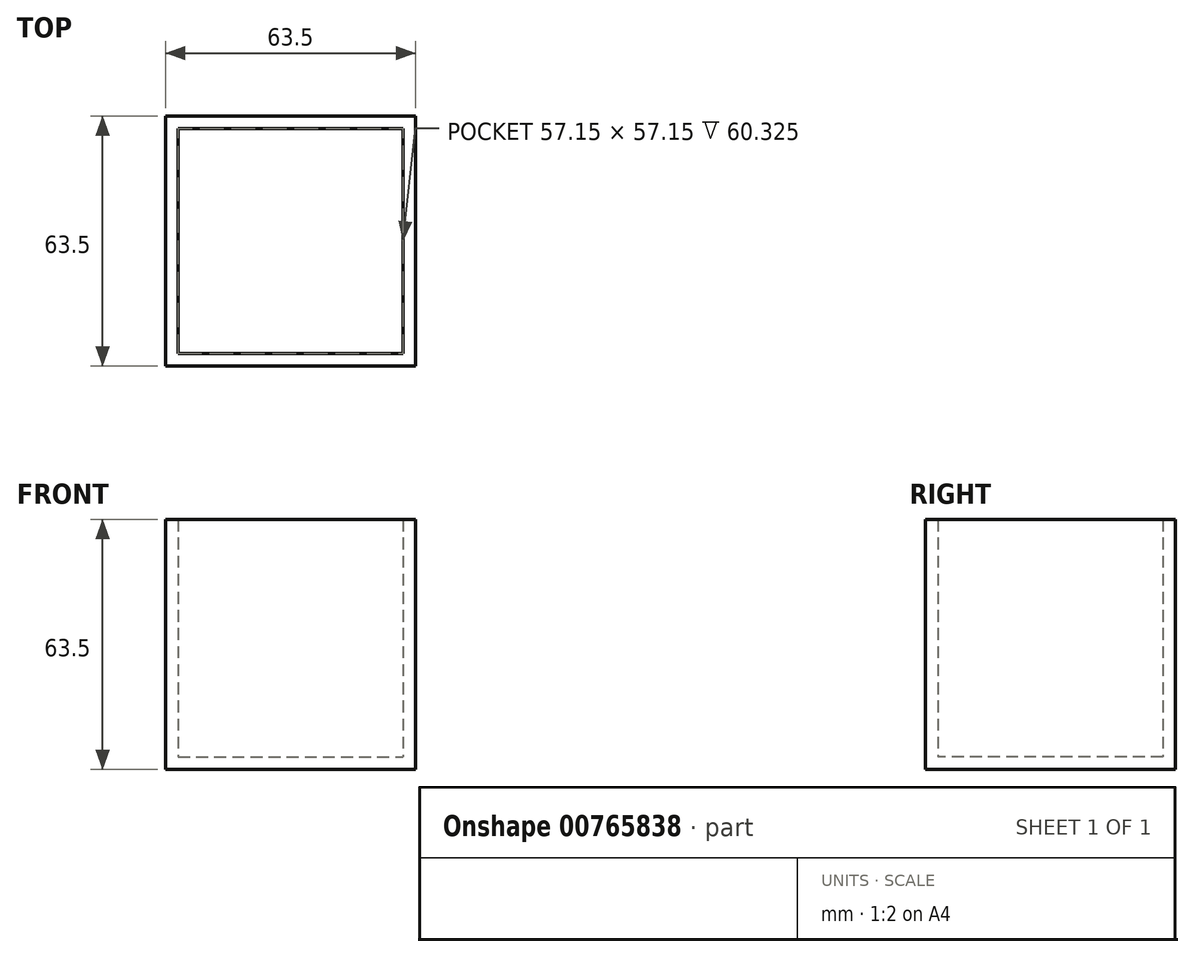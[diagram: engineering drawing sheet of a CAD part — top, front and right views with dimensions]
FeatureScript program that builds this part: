
annotation { "Feature Type Name" : "Feature", "Feature Type Description" : "" }
export const myFeature = defineFeature(function(context is Context, id is Id, definition is map)
    precondition{}
    {
        {
            var Q0;
            Q0=qCreatedBy(makeId("Top.planeOp"),FACE);
            var sketch = newSketch(context, id + "F0", { "sketchPlane" : qUnion([Q0])});
            skLineSegment(sketch, "E0.bottom", {"start": v(-31.75, 0) * mm, "end": v(31.75, 0) * mm});
            skLineSegment(sketch, "E0.top", {"start": v(-31.75, -63.5) * mm, "end": v(31.75, -63.5) * mm});
            skLineSegment(sketch, "E0.left", {"start": v(-31.75, 0) * mm, "end": v(-31.75, -63.5) * mm});
            skLineSegment(sketch, "E0.right", {"start": v(31.75, 0) * mm, "end": v(31.75, -63.5) * mm});
            skLineSegment(sketch, "E1", {"start": v(-31.75, -3.18) * mm, "end": v(31.75, -3.18) * mm});
            skLineSegment(sketch, "E2", {"start": v(-28.58, -3.18) * mm, "end": v(-28.57, -63.5) * mm});
            skLineSegment(sketch, "E3", {"start": v(28.58, -3.18) * mm, "end": v(28.58, -61.6) * mm});
            skLineSegment(sketch, "E4", {"start": v(-31.75, -60.33) * mm, "end": v(31.75, -60.33) * mm});
            skSolve(sketch);
        }
        {
            var Q0;
            {var subQ0=sQuery(id+"F0.wireOp",EDGE,"E2");var subQ1=sQuery(id+"F0.wireOp",EDGE,"E1");var subQ2=makeQuery(id+"F0.imprint","INTERSECT",VERTEX,{"derivedFrom":[subQ1,subQ0]});Q0=makeQuery(id+"F0.imprint","IMPRINT",FACE,{"disambiguationData":[TD([[makeQuery(id+"F0.imprint","IMPRINT",EDGE,{"disambiguationData":[TD([[subQ2,-1.0]])],"derivedFrom":subQ1}),-1.0]])]});}
            extrude(context, id + "F1", {"entities" : qUnion([Q0]), "depth" : 3.17 * mm, "offsetDistance" : 25.4 * mm});
        }
        {
            var Q0;
            {var subQ5=sQuery(id+"F0.wireOp",EDGE,"E0.bottom");Q0=makeQuery(id+"F0.imprint","IMPRINT",FACE,{"disambiguationData":[TD([[makeQuery(id+"F0.imprint","IMPRINT",EDGE,{"derivedFrom":subQ5}),-1.0]])]});}
            extrude(context, id + "F2", {"entities" : qUnion([Q0]), "operationType" : NewBodyOperationType.ADD, "depth" : 63.5 * mm, "offsetDistance" : 25.4 * mm});
        }
        {
            var Q0;
            {var subQ0=sQuery(id+"F0.wireOp",EDGE,"E1");var subQ1=sQuery(id+"F0.wireOp",EDGE,"E0.left");var subQ2=makeQuery(id+"F0.imprint","INTERSECT",VERTEX,{"derivedFrom":[subQ1,subQ0]});Q0=makeQuery(id+"F0.imprint","IMPRINT",FACE,{"disambiguationData":[TD([[makeQuery(id+"F0.imprint","IMPRINT",EDGE,{"disambiguationData":[TD([[subQ2,-1.0]])],"derivedFrom":subQ1}),1.0]])]});}
            var Q1;
            {var subQ0=sQuery(id+"F0.wireOp",EDGE,"E0.left");var subQ1=sQuery(id+"F0.wireOp",EDGE,"E0.top");var subQ2=makeQuery(id+"F0.imprint","INTERSECT",VERTEX,{"derivedFrom":[subQ1,subQ0]});Q1=makeQuery(id+"F0.imprint","IMPRINT",FACE,{"disambiguationData":[TD([[makeQuery(id+"F0.imprint","IMPRINT",EDGE,{"disambiguationData":[TD([[subQ2,-1.0]])],"derivedFrom":subQ1}),1.0]])]});}
            extrude(context, id + "F3", {"entities" : qUnion([Q0, Q1]), "operationType" : NewBodyOperationType.ADD, "depth" : 63.5 * mm, "offsetDistance" : 25.4 * mm});
        }
        {
            var Q0;
            {var subQ4=sQuery(id+"F0.wireOp",EDGE,"E0.top");var subQ6=sQuery(id+"F0.wireOp",EDGE,"E0.right");var subQ7=makeQuery(id+"F0.imprint","INTERSECT",VERTEX,{"derivedFrom":[subQ4,subQ6]});Q0=makeQuery(id+"F0.imprint","IMPRINT",FACE,{"disambiguationData":[TD([[makeQuery(id+"F0.imprint","IMPRINT",EDGE,{"disambiguationData":[TD([[subQ7,1.0]])],"derivedFrom":subQ4}),1.0]])]});}
            extrude(context, id + "F4", {"entities" : qUnion([Q0]), "operationType" : NewBodyOperationType.ADD, "depth" : 63.5 * mm, "offsetDistance" : 25.4 * mm});
        }
        {
            var Q0;
            {var subQ0=sQuery(id+"F0.wireOp",EDGE,"E1");var subQ1=sQuery(id+"F0.wireOp",EDGE,"E0.right");var subQ2=makeQuery(id+"F0.imprint","INTERSECT",VERTEX,{"derivedFrom":[subQ1,subQ0]});Q0=makeQuery(id+"F0.imprint","IMPRINT",FACE,{"disambiguationData":[TD([[makeQuery(id+"F0.imprint","IMPRINT",EDGE,{"disambiguationData":[TD([[subQ2,-1.0]])],"derivedFrom":subQ1}),-1.0]])]});}
            extrude(context, id + "F5", {"entities" : qUnion([Q0]), "operationType" : NewBodyOperationType.ADD, "depth" : 63.5 * mm, "offsetDistance" : 25.4 * mm});
        }
    });
